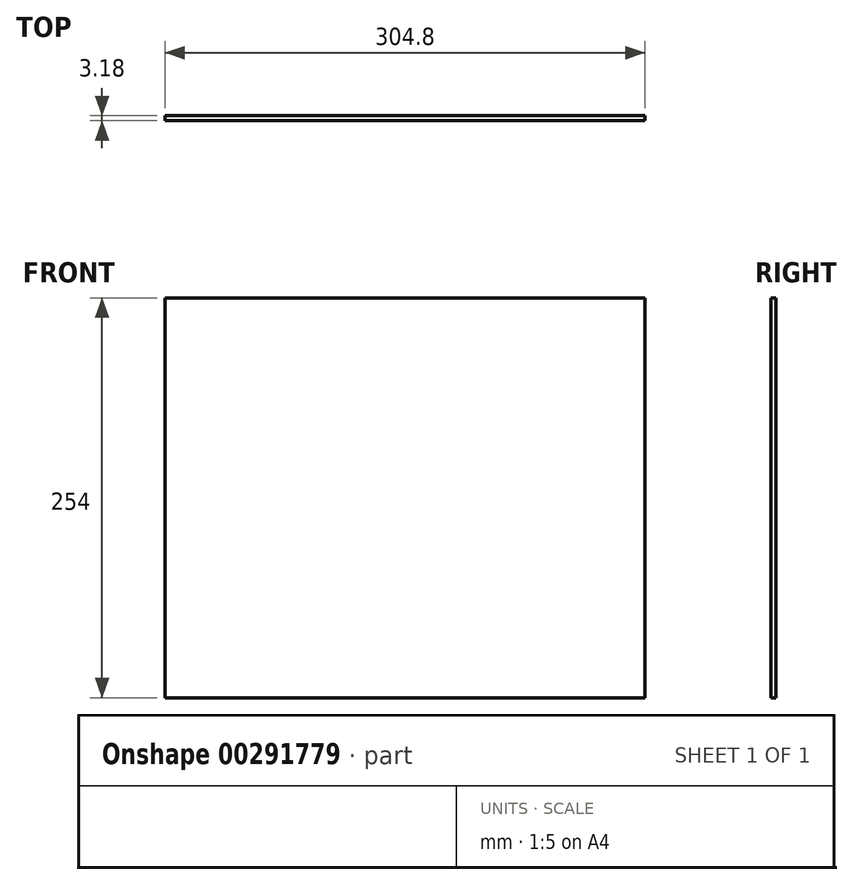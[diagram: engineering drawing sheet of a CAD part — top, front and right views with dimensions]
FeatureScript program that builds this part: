
annotation { "Feature Type Name" : "Feature", "Feature Type Description" : "" }
export const myFeature = defineFeature(function(context is Context, id is Id, definition is map)
    precondition{}
    {
        {
            var Q0;
            Q0=qCreatedBy(makeId("Front.planeOp"),FACE);
            var sketch = newSketch(context, id + "F0", { "sketchPlane" : qUnion([Q0])});
            skLineSegment(sketch, "E0.bottom", {"start": v(-457.2, -215.56) * mm, "end": v(-152.4, -215.56) * mm});
            skLineSegment(sketch, "E0.top", {"start": v(-457.2, -469.56) * mm, "end": v(-152.4, -469.56) * mm});
            skLineSegment(sketch, "E0.left", {"start": v(-457.2, -215.56) * mm, "end": v(-457.2, -469.56) * mm});
            skLineSegment(sketch, "E0.right", {"start": v(-152.4, -215.56) * mm, "end": v(-152.4, -469.56) * mm});
            skSolve(sketch);
        }
        {
            var Q0;
            Q0=makeQuery(id+"F0.imprint","IMPRINT",FACE,{"disambiguationData":[TD([[makeQuery(id+"F0.imprint","IMPRINT",EDGE,{"derivedFrom":sQuery(id+"F0.wireOp",EDGE,"E0.bottom")}),-1.0]])]});
            extrude(context, id + "F1", {"entities" : qUnion([Q0]), "endBound" : BoundingType.SYMMETRIC, "depth" : 3.17 * mm});
        }
    });
